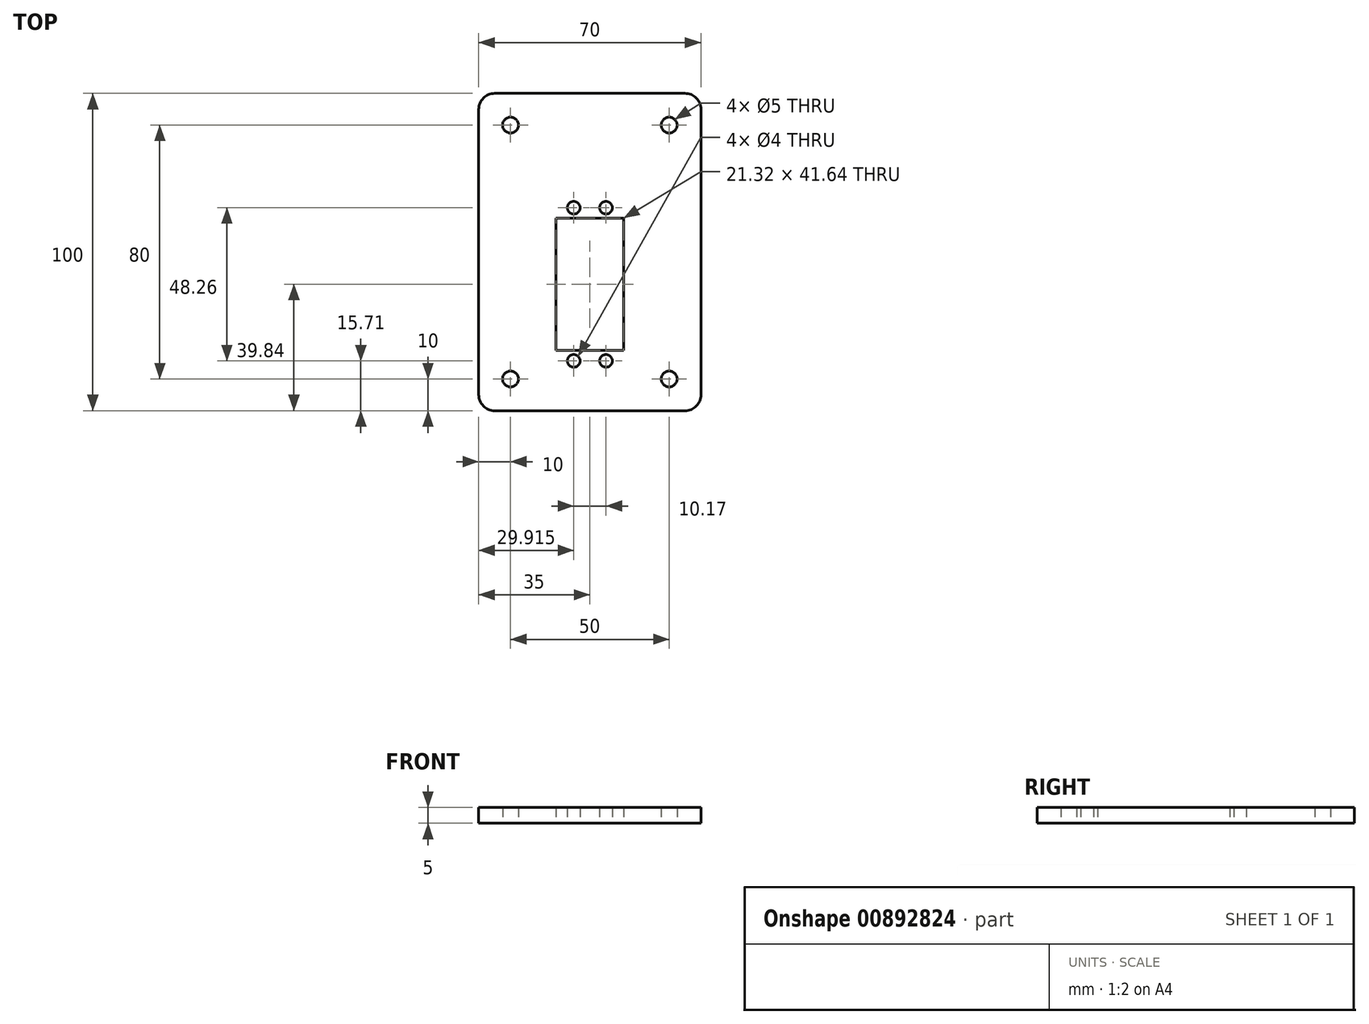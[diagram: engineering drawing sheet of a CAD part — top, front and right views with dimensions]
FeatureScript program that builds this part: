
annotation { "Feature Type Name" : "Feature", "Feature Type Description" : "" }
export const myFeature = defineFeature(function(context is Context, id is Id, definition is map)
    precondition{}
    {
        {
            var Q0;
            Q0=qCreatedBy(makeId("Top.planeOp"),FACE);
            var sketch = newSketch(context, id + "F0", { "sketchPlane" : qUnion([Q0])});
            skLineSegment(sketch, "E0", {"start": v(-5.08, 13.97) * mm, "end": v(5.08, 13.97) * mm, "construction": true});
            skLineSegment(sketch, "E1", {"start": v(-5.08, -34.3) * mm, "end": v(5.09, -34.3) * mm, "construction": true});
            skCircle(sketch, "E2", {"center": v(0, 0) * mm, "radius": 22.5 * mm, "construction": true});
            skCircle(sketch, "E3", {"center": v(0, 0) * mm, "radius": 30 * mm, "construction": true});
            skLineSegment(sketch, "E4.bottom", {"start": v(-30, 50) * mm, "end": v(30, 50) * mm});
            skLineSegment(sketch, "E4.top", {"start": v(-30, -50) * mm, "end": v(30, -50) * mm});
            skLineSegment(sketch, "E4.left", {"start": v(-35, 45) * mm, "end": v(-35, -45) * mm});
            skLineSegment(sketch, "E4.right", {"start": v(35, 45) * mm, "end": v(35, -45) * mm});
            skLineSegment(sketch, "E5", {"start": v(-35, 0) * mm, "end": v(35, 0) * mm, "construction": true});
            skLineSegment(sketch, "E6", {"start": v(0, -50) * mm, "end": v(0, 50) * mm, "construction": true});
            skLineSegment(sketch, "E7", {"start": v(-25, 50) * mm, "end": v(-25, -50) * mm, "construction": true});
            skLineSegment(sketch, "E8", {"start": v(-35, 40) * mm, "end": v(35, 40) * mm, "construction": true});
            skLineSegment(sketch, "E9.MirrorCS", {"start": v(-35, -40) * mm, "end": v(35, -40) * mm, "construction": true});
            skLineSegment(sketch, "E10.MirrorCS", {"start": v(25, 50) * mm, "end": v(25, -50) * mm, "construction": true});
            skLineSegment(sketch, "E11.trimOffspring", {"start": v(-5.08, 13.97) * mm, "end": v(-5.08, -34.3) * mm, "construction": true});
            skCircle(sketch, "E12", {"center": v(-25, 40) * mm, "radius": 2.5 * mm});
            skCircle(sketch, "E13", {"center": v(25, 40) * mm, "radius": 2.5 * mm});
            skCircle(sketch, "E14", {"center": v(25, -40) * mm, "radius": 2.5 * mm});
            skCircle(sketch, "E15", {"center": v(-25, -40) * mm, "radius": 2.5 * mm});
            skCircle(sketch, "E16", {"center": v(-5.08, 13.97) * mm, "radius": 2 * mm});
            skCircle(sketch, "E17", {"center": v(5.08, 13.97) * mm, "radius": 2 * mm});
            skCircle(sketch, "E18", {"center": v(-5.08, -34.3) * mm, "radius": 2 * mm});
            skCircle(sketch, "E19", {"center": v(5.09, -34.3) * mm, "radius": 2 * mm});
            skLineSegment(sketch, "E20.bottom", {"start": v(-10.16, 10.16) * mm, "end": v(10.16, 10.16) * mm});
            skLineSegment(sketch, "E20.top", {"start": v(-10.16, -30.48) * mm, "end": v(10.16, -30.48) * mm});
            skLineSegment(sketch, "E20.left", {"start": v(-10.16, 10.16) * mm, "end": v(-10.16, -30.48) * mm});
            skLineSegment(sketch, "E20.right", {"start": v(10.16, 10.16) * mm, "end": v(10.16, -30.48) * mm});
            skPoint(sketch, "E21.visualSharp", {"position": v(-35, 50) * mm});
            skArc(sketch, "E21.filletArc", {"start": v(-30, 50) * mm, "mid": v(-33.54, 48.54) * mm, "end": v(-35, 45) * mm});
            skPoint(sketch, "E22.visualSharp", {"position": v(35, 50) * mm});
            skArc(sketch, "E22.filletArc", {"start": v(35, 45) * mm, "mid": v(33.54, 48.54) * mm, "end": v(30, 50) * mm});
            skPoint(sketch, "E23.visualSharp", {"position": v(35, -50) * mm});
            skArc(sketch, "E23.filletArc", {"start": v(30, -50) * mm, "mid": v(33.54, -48.54) * mm, "end": v(35, -45) * mm});
            skPoint(sketch, "E24.visualSharp", {"position": v(-35, -50) * mm});
            skArc(sketch, "E24.filletArc", {"start": v(-35, -45) * mm, "mid": v(-33.54, -48.54) * mm, "end": v(-30, -50) * mm});
            skLineSegment(sketch, "E25", {"start": v(5.08, 13.97) * mm, "end": v(5.08, 10.16) * mm, "construction": true});
            skLineSegment(sketch, "E26", {"start": v(5.09, -30.48) * mm, "end": v(5.09, -34.3) * mm, "construction": true});
            skLineSegment(sketch, "E27.0", {"start": v(-10.66, 10.66) * mm, "end": v(10.66, 10.66) * mm});
            skLineSegment(sketch, "E27.1", {"start": v(-10.66, 10.66) * mm, "end": v(-10.66, -30.98) * mm});
            skLineSegment(sketch, "E27.2", {"start": v(-10.66, -30.98) * mm, "end": v(10.66, -30.98) * mm});
            skLineSegment(sketch, "E27.3", {"start": v(10.66, 10.66) * mm, "end": v(10.66, -30.98) * mm});
            skSolve(sketch);
        }
        {
            var Q0;
            Q0=makeQuery(id+"F0.imprint","IMPRINT",FACE,{"disambiguationData":[TD([[makeQuery(id+"F0.imprint","IMPRINT",EDGE,{"derivedFrom":sQuery(id+"F0.wireOp",EDGE,"E4.bottom")}),-1.0]])]});
            extrude(context, id + "F1", {"entities" : qUnion([Q0]), "depth" : 5 * mm, "offsetDistance" : 25 * mm});
        }
    });
